FCSTD DOCUMENT  (FreeCAD 0.19R23578 (Git))
Label: printer_assembly_v2
License: All rights reserved
LicenseURL: http://en.wikipedia.org/wiki/All_rights_reserved
objects: App::Link×4, PartDesign::CoordinateSystem×1, App::DocumentObjectGroup×1, App::FeaturePython×1, App::Part×1
note: 1 computed .brp shape members not serialized (recipe doc carries the construction recipe); baked Part::Feature solids carry a one-line shape summary decoded from their .brp
EXTERNAL_REF file=base_plate.FCStd obj=LCS_2
EXTERNAL_REF file=base_plate.FCStd obj=Part014
EXTERNAL_REF file=base_plate.FCStd obj=LCS_1
EXTERNAL_REF file=frame_assembly.FCStd obj=LCS_Origin
EXTERNAL_REF file=frame_assembly.FCStd obj=Model
EXTERNAL_REF file=z_axis_assembly.FCStd obj=Model
EXTERNAL_REF file=enclosure_assembly.FCStd obj=LCS_Origin
EXTERNAL_REF file=enclosure_assembly.FCStd obj=Model

FEATURE [PartDesign::CoordinateSystem] LCS_Origin
  AttacherType = Attacher::AttachEngine3D
  MapMode = 2
  Support = -> [X_Axis]
FEATURE [App::DocumentObjectGroup] Constraints
FEATURE [App::FeaturePython] Variables  # WARN: FeaturePython — macro-defined, semantics opaque (R4)
FEATURE [App::Link] base_plate_base_plate
  AssemblyType = Asm4EE
  AttachedBy = #LCS_2
  AttachedTo = Parent Assembly#LCS_Origin
  AttachmentOffset = pos=(0,0,0) rot=(0,0,1;1.5708rad)
  LinkPlacement = pos=(-164.998,0.0367946,19.05) rot=(0,0,-1;0.00036rad)
  LinkedObject = -> <external base_plate.FCStd>#Part014
  Placement = pos=(-164.998,0.0367946,19.05) rot=(0,0,-1;0.00036rad)
  expr: Placement = LCS_Origin.Placement * AttachmentOffset * base_plate#LCS_2.Placement ^ -1
FEATURE [App::Link] frame_assembly
  AssemblyType = Asm4EE
  AttachedBy = #LCS_Origin
  AttachedTo = base_plate_base_plate#LCS_1
  AttachmentOffset = pos=(0,0,0) rot=(0,-0.707107,-0.707107;3.14159rad)
  LinkPlacement = pos=(-139.598,0.0276527,19.05) rot=(0,0,-1;0.00036rad)
  LinkedObject = -> <external frame_assembly.FCStd>#Model
  Placement = pos=(-139.598,0.0276527,19.05) rot=(0,0,-1;0.00036rad)
  expr: Placement = base_plate_base_plate.Placement * base_plate#LCS_1.Placement * AttachmentOffset * frame_assembly#LCS_Origin.Placement ^ -1
FEATURE [App::Link] z_axis_assembly
  LinkPlacement = pos=(-139.598,0.0275961,256.05) rot=(0.000331,0,-1;0.00036rad)
  LinkedObject = -> <external z_axis_assembly.FCStd>#Model
  Placement = pos=(-139.598,0.0275961,256.05) rot=(0.000331,0,-1;0.00036rad)
FEATURE [App::Link] enclosure_assembly
  AssemblyType = Asm4EE
  AttachedBy = #LCS_Origin
  AttachedTo = Parent Assembly#LCS_Origin
  AttachmentOffset = pos=(-166,0,20) rot=(0,0,1;0rad)
  LinkPlacement = pos=(-166,0,20) rot=(0,0,1;0rad)
  LinkedObject = -> <external enclosure_assembly.FCStd>#Model
  Placement = pos=(-166,0,20) rot=(0,0,1;0rad)
  expr: Placement = LCS_Origin.Placement * AttachmentOffset * enclosure_assembly#LCS_Origin.Placement ^ -1
FEATURE [App::Part] Model
  Configuration = 0
  Group = -> [LCS_Origin,Constraints,Variables,base_plate_base_plate,frame_assembly,z_axis_assembly,enclosure_assembly]
  Origin = -> Origin
  Type = Assembly4 Model

RESOLVED EXTERNAL PARTS (link-assembly join: the EXTERNAL_REF files above that resolve inside this repo's crawl, each included once):
---- part base_plate.FCStd = doc fcstd_9e080127ff6f ----
FCSTD DOCUMENT  (FreeCAD 0.19R23578 (Git))
Label: base_plate
License: All rights reserved
LicenseURL: http://en.wikipedia.org/wiki/All_rights_reserved
objects: Sketcher::SketchObject×5, PartDesign::Pocket×3, PartDesign::Pad×2, PartDesign::CoordinateSystem×2, PartDesign::Body×1, App::Part×1
note: 18 computed .brp shape members not serialized (recipe doc carries the construction recipe); baked Part::Feature solids carry a one-line shape summary decoded from their .brp

FEATURE [Sketcher::SketchObject] Sketch018
  MapMode = 5
  Support = -> [XY_Plane021]
  sketch-geometry (4):
    g0: LineSegment StartX=-63.5 StartY=177.8 StartZ=0 EndX=393.7 EndY=177.8 EndZ=0
    g1: LineSegment StartX=393.7 StartY=177.8 StartZ=0 EndX=393.7 EndY=-177.8 EndZ=0
    g2: LineSegment StartX=393.7 StartY=-177.8 StartZ=0 EndX=-63.5 EndY=-177.8 EndZ=0
    g3: LineSegment StartX=-63.5 StartY=-177.8 StartZ=0 EndX=-63.5 EndY=177.8 EndZ=0
  constraints (11):
    c: Coincident(g0,g1)
    c: Coincident(g1,g2)
    c: Coincident(g2,g3)
    c: Coincident(g3,g0)
    c: Horizontal(g0)
    c: Horizontal(g2)
    c: Vertical(g1)
    c: DistanceY(g-1,g0) = 177.8
    c: DistanceX(g0,g0) = 457.2
    c: DistanceX(g0,g-1) = 63.5
    c: Symmetric(g0,g2,g-1)
FEATURE [PartDesign::Pad] Pad008
  AllowMultiFace = false
  Direction = (1,1,1)
  Length = 19.05
  Length2 = 100
  Profile = -> Sketch018
  Reversed = true
  Type = 0
FEATURE [Sketcher::SketchObject] Sketch019
  MapMode = 5
  Support = -> [XY_Plane021]
  sketch-geometry (12):
    g0: LineSegment StartX=0 StartY=-127 StartZ=0 EndX=0 EndY=-177.8 EndZ=0
    g1: LineSegment StartX=0 StartY=-177.8 StartZ=0 EndX=-12.7 EndY=-177.8 EndZ=0
    g2: LineSegment StartX=-12.7 StartY=-177.8 StartZ=0 EndX=-12.7 EndY=-136.525 EndZ=0
    g3: LineSegment StartX=-63.5 StartY=-127 StartZ=0 EndX=-63.5 EndY=-136.525 EndZ=0
    g4: LineSegment StartX=-63.5 StartY=-136.525 StartZ=0 EndX=-12.7 EndY=-136.525 EndZ=0
    g5: LineSegment StartX=-63.5 StartY=-127 StartZ=0 EndX=0 EndY=-127 EndZ=0
    g6: LineSegment StartX=-12.7 StartY=136.525 StartZ=0 EndX=-63.5 EndY=136.525 EndZ=0
    g7: LineSegment StartX=-63.5 StartY=136.525 StartZ=0 EndX=-63.5 EndY=127 EndZ=0
    g8: LineSegment StartX=-63.5 StartY=127 StartZ=0 EndX=0 EndY=127 EndZ=0
    g9: LineSegment StartX=0 StartY=127 StartZ=0 EndX=0 EndY=177.8 EndZ=0
    g10: LineSegment StartX=0 StartY=177.8 StartZ=0 EndX=-12.7 EndY=177.8 EndZ=0
    g11: LineSegment StartX=-12.7 StartY=177.8 StartZ=0 EndX=-12.7 EndY=136.525 EndZ=0
  constraints (36):
    c: Coincident(g0,g1)
    c: Coincident(g1,g2)
    c: Horizontal(g1)
    c: Vertical(g0)
    c: Vertical(g2)
    c: Coincident(g3,g4)
    c: Horizontal(g4)
    c: Vertical(g3)
    c: Coincident(g2,g4)
    c: Coincident(g5,g3)
    c: Coincident(g5,g0)
    c: Horizontal(g5)
    c: DistanceY(g0,g-1) = 177.8
    c: DistanceX(g5,g5) = 63.5
    c: DistanceY(g3,g3) = 9.525
    c: PointOnObject(g0,g-2)
    c: DistanceY(g0,g0) = 50.8
    c: DistanceX(g1,g1) = 12.7
    c: Horizontal(g6)
    c: Coincident(g6,g7)
    c: Coincident(g7,g8)
    c: Coincident(g8,g9)
    c: Coincident(g9,g10)
    c: Coincident(g10,g11)
    c: Coincident(g11,g6)
    c: Vertical(g11)
    c: Vertical(g9)
    c: Vertical(g7)
    c: Horizontal(g10)
    c: Horizontal(g8)
    c: PointOnObject(g8,g-2)
    c: DistanceX(g10,g10) = 12.7
    c: DistanceX(g8,g8) = 63.5
    c: DistanceY(g9,g9) = 50.8
    c: DistanceY(g7,g7) = 9.525
    c: DistanceY(g-1,g9) = 177.8
FEATURE [PartDesign::Pad] Pad009
  AllowMultiFace = false
  BaseFeature = -> Pad008
  Direction = (1,1,1)
  Length = 127
  Length2 = 100
  Profile = -> Sketch019
  Type = 0
FEATURE [Sketcher::SketchObject] Sketch020
  MapMode = 5
  Placement = pos=(0,0,0) rot=(1,0,0;1.5708rad)
  Support = -> [XZ_Plane021]
  sketch-geometry (3):
    g0: LineSegment StartX=-63.5 StartY=0 StartZ=0 EndX=-12.7 EndY=127 EndZ=0
    g1: LineSegment StartX=-12.7 StartY=127 StartZ=0 EndX=-63.5 EndY=127 EndZ=0
    g2: LineSegment StartX=-63.5 StartY=127 StartZ=0 EndX=-63.5 EndY=0 EndZ=0
  constraints (9):
    c: Coincident(g0,g1)
    c: Horizontal(g1)
    c: Coincident(g1,g2)
    c: Coincident(g2,g0)
    c: Vertical(g2)
    c: PointOnObject(g0,g-1)
    c: DistanceY(g2,g2) = 127
    c: DistanceX(g0,g-1) = 12.7
    c: DistanceX(g0,g-1) = 63.5
FEATURE [PartDesign::Pocket] Pocket010
  AllowMultiFace = false
  BaseFeature = -> Pad009
  Length = 5
  Length2 = 100
  Midplane = true
  Profile = -> Sketch020
  Type = 1
FEATURE [Sketcher::SketchObject] Sketch021
  MapMode = 5
  Placement = pos=(0,0,0) rot=(0.57735,0.57735,0.57735;2.0944rad)
  Support = -> [YZ_Plane021]
  sketch-geometry (4):
    g0: Circle CenterX=-152.4 CenterY=101.6 CenterZ=0 NormalX=0 NormalY=0 NormalZ=1 AngleXU=0 Radius=6.35
    g1: Circle CenterX=-152.4 CenterY=25.4 CenterZ=0 NormalX=0 NormalY=0 NormalZ=1 AngleXU=0 Radius=6.35
    g2: Circle CenterX=152.4 CenterY=101.6 CenterZ=0 NormalX=0 NormalY=0 NormalZ=1 AngleXU=0 Radius=6.35
    g3: Circle CenterX=152.4 CenterY=25.4 CenterZ=0 NormalX=0 NormalY=0 NormalZ=1 AngleXU=0 Radius=6.35
  constraints (10):
    c: Symmetric(g1,g3,g-2)
    c: Symmetric(g0,g2,g-2)
    c: DistanceX(g0,g-1) = 152.4
    c: Vertical(g0,g1)
    c: Diameter(g0) = 12.7
    c: Equal(g0,g1)
    c: Equal(g1,g3)
    c: Equal(g3,g2)
    c: DistanceY(g-1,g0) = 101.6
    c: DistanceY(g-1,g1) = 25.4
FEATURE [PartDesign::Pocket] Pocket009
  AllowMultiFace = false
  BaseFeature = -> Pocket010
  Length = 5
  Length2 = 100
  Profile = -> Sketch021
  Type = 1
FEATURE [Sketcher::SketchObject] Sketch095
  MapMode = 5
  Support = -> [XY_Plane021]
  sketch-geometry (3):
    g0: Circle CenterX=245 CenterY=44 CenterZ=0 NormalX=0 NormalY=0 NormalZ=1 AngleXU=0 Radius=4
    g1: Circle CenterX=335 CenterY=-24 CenterZ=0 NormalX=0 NormalY=0 NormalZ=1 AngleXU=0 Radius=4
    g2: Circle CenterX=245 CenterY=-93 CenterZ=0 NormalX=0 NormalY=0 NormalZ=1 AngleXU=0 Radius=4
  constraints (9):
    c: Equal(g2,g0)
    c: Equal(g0,g1)
    c: Diameter(g1) = 8
    c: Vertical(g2,g0)
    c: DistanceY(g-1,g0) = 44
    c: DistanceX(g-1,g0) = 245
    c: DistanceY(g2,g-1) = 93
    c: DistanceX(g-1,g1) = 335
    c: DistanceY(g1,g-1) = 24
FEATURE [PartDesign::Pocket] Pocket
  BaseFeature = -> Pocket009
  Length = 5
  Length2 = 100
  Midplane = true
  Profile = -> Sketch095
  Type = 1
FEATURE [PartDesign::Body] Body008  label="Body"
  Group = -> [Sketch018,Pad008,Sketch019,Pad009,Sketch020,Pocket010,Sketch021,Pocket009,Sketch095,Pocket]
  Origin = -> Origin021
  Tip = -> Pocket
FEATURE [PartDesign::CoordinateSystem] LCS_1
  AttacherType = Attacher::AttachEngine3D
  AttachmentOffset = pos=(-25.4,0,0) rot=(0,0,1;0rad)
  MapMode = 45
  Placement = pos=(25.4,0,0) rot=(0,0.707107,0.707107;3.14159rad)
  Support = -> [Pocket]
FEATURE [PartDesign::CoordinateSystem] LCS_2
  AttacherType = Attacher::AttachEngine3D
  MapMode = 45
  Placement = pos=(164.998,0.0225906,-19.05) rot=(0,0,1;1.57116rad)
  Support = -> [Pocket]
FEATURE [App::Part] Part014  label="base_plate"
  Group = -> [Body008,LCS_1,LCS_2]
  Origin = -> Origin020
---- part enclosure_assembly.FCStd = doc fcstd_0174c90f82aa ----
FCSTD DOCUMENT  (FreeCAD 0.19R23578 (Git))
Label: enclosure_assembly
License: All rights reserved
LicenseURL: http://en.wikipedia.org/wiki/All_rights_reserved
objects: App::Link×8, App::DocumentObjectGroup×2, PartDesign::CoordinateSystem×1, App::FeaturePython×1, App::Part×1
note: 1 computed .brp shape members not serialized (recipe doc carries the construction recipe); baked Part::Feature solids carry a one-line shape summary decoded from their .brp
EXTERNAL_REF file=enclosure_sheetmetal.FCStd obj=LCS_4
EXTERNAL_REF file=enclosure_sheetmetal.FCStd obj=Body
EXTERNAL_REF file=enclosure_sheetmetal.FCStd obj=LCS_5
EXTERNAL_REF file=enclosure_windows.FCStd obj=LCS_1
EXTERNAL_REF file=enclosure_windows.FCStd obj=Body001
EXTERNAL_REF file=enclosure_hinges.FCStd obj=LCS_1
EXTERNAL_REF file=enclosure_sheetmetal.FCStd obj=LCS_7
EXTERNAL_REF file=enclosure_hinges.FCStd obj=Body001
EXTERNAL_REF file=enclosure_sheetmetal.FCStd obj=LCS_6
EXTERNAL_REF file=enclosure_hinges.FCStd obj=LCS_4
EXTERNAL_REF file=enclosure_hinges.FCStd obj=LCS_7
EXTERNAL_REF file=enclosure_hinges.FCStd obj=Body002
EXTERNAL_REF file=enclosure_hinges.FCStd obj=LCS_6
EXTERNAL_REF file=enclosure_sheetmetal.FCStd obj=LCS_3
EXTERNAL_REF file=enclosure_sheetmetal.FCStd obj=LCS_2
EXTERNAL_REF file=enclosure_sheetmetal.FCStd obj=Body001
EXTERNAL_REF file=enclosure_sheetmetal.FCStd obj=LCS_1
EXTERNAL_REF file=enclosure_windows.FCStd obj=LCS_2
EXTERNAL_REF file=enclosure_windows.FCStd obj=Body

FEATURE [App::DocumentObjectGroup] Parts
FEATURE [PartDesign::CoordinateSystem] LCS_Origin
  AttacherType = Attacher::AttachEngine3D
  MapMode = 2
  Support = -> [X_Axis]
FEATURE [App::DocumentObjectGroup] Constraints
FEATURE [App::FeaturePython] Variables  # WARN: FeaturePython — macro-defined, semantics opaque (R4)
FEATURE [App::Link] enclosure_sheetmetal_main_housing
  AssemblyType = Asm4EE
  AttachedBy = #LCS_4
  AttachedTo = Parent Assembly#LCS_Origin
  AttachmentOffset = pos=(0,0,0) rot=(0.707107,0,0.707107;3.14159rad)
  LinkPlacement = pos=(0,304.8,-3.73e-14) rot=(0.707107,0,0.707107;3.14159rad)
  LinkedObject = -> <external enclosure_sheetmetal.FCStd>#Body
  Placement = pos=(0,304.8,-3.73e-14) rot=(0.707107,0,0.707107;3.14159rad)
  expr: Placement = LCS_Origin.Placement * AttachmentOffset * enclosure_sheetmetal#LCS_4.Placement ^ -1
FEATURE [App::Link] enclosure_windows_top_acrylic_panel
  AssemblyType = Asm4EE
  AttachedBy = #LCS_1
  AttachedTo = enclosure_sheetmetal_main_housing#LCS_5
  AttachmentOffset = pos=(0,0,0) rot=(0,0,1;1.5708rad)
  LinkPlacement = pos=(298,2.6933e-12,573.5) rot=(0,0,-1;4.71239rad)
  LinkedObject = -> <external enclosure_windows.FCStd>#Body001
  Placement = pos=(298,2.6933e-12,573.5) rot=(0,0,-1;4.71239rad)
  expr: Placement = enclosure_sheetmetal_main_housing.Placement * enclosure_sheetmetal#LCS_5.Placement * AttachmentOffset * enclosure_windows#LCS_1.Placement ^ -1
FEATURE [App::Link] enclosure_hinges_Hinge_A
  AssemblyType = Asm4EE
  AttachedBy = #LCS_1
  AttachedTo = enclosure_sheetmetal_main_housing#LCS_7
  LinkPlacement = pos=(107.95,-306.8,514.35) rot=(-1,0,0;4.71239rad)
  LinkedObject = -> <external enclosure_hinges.FCStd>#Body001
  Placement = pos=(107.95,-306.8,514.35) rot=(-1,0,0;4.71239rad)
  expr: Placement = enclosure_sheetmetal_main_housing.Placement * enclosure_sheetmetal#LCS_7.Placement * AttachmentOffset * enclosure_hinges#LCS_1.Placement ^ -1
FEATURE [App::Link] enclosure_hinges_Hinge_A001
  AssemblyType = Asm4EE
  AttachedBy = #LCS_1
  AttachedTo = enclosure_sheetmetal_main_housing#LCS_6
  LinkPlacement = pos=(107.95,-306.8,95.25) rot=(-1,0,0;4.71239rad)
  LinkedObject = -> <external enclosure_hinges.FCStd>#Body001
  Placement = pos=(107.95,-306.8,95.25) rot=(-1,0,0;4.71239rad)
  expr: Placement = enclosure_sheetmetal_main_housing.Placement * enclosure_sheetmetal#LCS_6.Placement * AttachmentOffset * enclosure_hinges#LCS_1.Placement ^ -1
FEATURE [App::Link] enclosure_hinges_Hinge_B
  AssemblyType = Asm4EE
  AttachedBy = #LCS_7
  AttachedTo = enclosure_hinges_Hinge_A#LCS_4
  LinkPlacement = pos=(127,-325.85,476.25) rot=(0.57735,0.57735,-0.57735;4.18879rad)
  LinkedObject = -> <external enclosure_hinges.FCStd>#Body002
  Placement = pos=(127,-325.85,476.25) rot=(0.57735,0.57735,-0.57735;4.18879rad)
  expr: Placement = enclosure_hinges_Hinge_A.Placement * enclosure_hinges#LCS_4.Placement * AttachmentOffset * enclosure_hinges#LCS_7.Placement ^ -1
FEATURE [App::Link] enclosure_hinges_Hinge_B001
  AssemblyType = Asm4EE
  AttachedBy = #LCS_6
  AttachedTo = enclosure_sheetmetal_door#LCS_3
  AttachmentOffset = pos=(0,0,0) rot=(1,0,0;3.14159rad)
  LinkPlacement = pos=(127,-325.85,57.15) rot=(-0.57735,-0.57735,0.57735;2.0944rad)
  LinkedObject = -> <external enclosure_hinges.FCStd>#Body002
  Placement = pos=(127,-325.85,57.15) rot=(-0.57735,-0.57735,0.57735;2.0944rad)
  expr: Placement = enclosure_sheetmetal_door.Placement * enclosure_sheetmetal#LCS_3.Placement * AttachmentOffset * enclosure_hinges#LCS_6.Placement ^ -1
FEATURE [App::Link] enclosure_sheetmetal_door
  AssemblyType = Asm4EE
  AttachedBy = #LCS_2
  AttachedTo = enclosure_hinges_Hinge_B#LCS_6
  AttachmentOffset = pos=(0,0,0) rot=(1,0,0;3.14159rad)
  LinkPlacement = pos=(129,-346.9,571.5) rot=(1,0,0;4.71239rad)
  LinkedObject = -> <external enclosure_sheetmetal.FCStd>#Body001
  Placement = pos=(129,-346.9,571.5) rot=(1,0,0;4.71239rad)
  expr: Placement = enclosure_hinges_Hinge_B.Placement * enclosure_hinges#LCS_6.Placement * AttachmentOffset * enclosure_sheetmetal#LCS_2.Placement ^ -1
FEATURE [App::Link] enclosure_windows_side_acrylic_panel
  AssemblyType = Asm4EE
  AttachedBy = #LCS_2
  AttachedTo = enclosure_sheetmetal_door#LCS_1
  AttachmentOffset = pos=(0,0,0) rot=(0,0,1;3.14159rad)
  LinkPlacement = pos=(757.6,-346.9,284.75) rot=(0,-0.707107,-0.707107;3.14159rad)
  LinkedObject = -> <external enclosure_windows.FCStd>#Body
  Placement = pos=(757.6,-346.9,284.75) rot=(0,-0.707107,-0.707107;3.14159rad)
  expr: Placement = enclosure_sheetmetal_door.Placement * enclosure_sheetmetal#LCS_1.Placement * AttachmentOffset * enclosure_windows#LCS_2.Placement ^ -1
FEATURE [App::Part] Model
  Configuration = 0
  Group = -> [LCS_Origin,Constraints,Variables,enclosure_sheetmetal_main_housing,enclosure_windows_top_acrylic_panel,enclosure_hinges_Hinge_A,enclosure_hinges_Hinge_A001,enclosure_hinges_Hinge_B,enclosure_hinges_Hinge_B001,enclosure_sheetmetal_door,enclosure_windows_side_acrylic_panel]
  Origin = -> Origin
  Type = Assembly4 Model
---- part frame_assembly.FCStd = doc fcstd_40f002513768 ----
FCSTD DOCUMENT  (FreeCAD 0.19R23578 (Git))
Label: frame_assembly
License: All rights reserved
LicenseURL: http://en.wikipedia.org/wiki/All_rights_reserved
objects: App::Link×11, App::DocumentObjectGroup×2, PartDesign::CoordinateSystem×1, App::FeaturePython×1, App::Part×1
note: 1 computed .brp shape members not serialized (recipe doc carries the construction recipe); baked Part::Feature solids carry a one-line shape summary decoded from their .brp
EXTERNAL_REF file=frame_bottom_piece.FCStd obj=LCS_4
EXTERNAL_REF file=frame_bottom_piece.FCStd obj=Part008
EXTERNAL_REF file=frame_bottom_piece.FCStd obj=LCS_2
EXTERNAL_REF file=frame_side_piece.FCStd obj=LCS_2
EXTERNAL_REF file=frame_side_piece.FCStd obj=Part006
EXTERNAL_REF file=frame_bottom_piece.FCStd obj=LCS_1
EXTERNAL_REF file=frame_side_piece.FCStd obj=LCS_1
EXTERNAL_REF file=frame_top_piece.FCStd obj=LCS_2
EXTERNAL_REF file=frame_top_piece.FCStd obj=Part007
EXTERNAL_REF file=frame_top_piece.FCStd obj=LCS_3
EXTERNAL_REF file=z_motor_adaptor_plate.FCStd obj=LCS_1
EXTERNAL_REF file=z_motor_adaptor_plate.FCStd obj=Part
EXTERNAL_REF file=Nema 17  Stepper Motor length 60mm.FcStd obj=LCS_0
EXTERNAL_REF file=z_motor_adaptor_plate.FCStd obj=LCS_2
EXTERNAL_REF file=Nema 17  Stepper Motor length 60mm.FcStd obj=Part
EXTERNAL_REF file=Nema 17  Stepper Motor length 60mm.FcStd obj=LCS_1
EXTERNAL_REF file=5to8mm_spider_coupler.FCStd obj=LCS_1
EXTERNAL_REF file=5to8mm_spider_coupler.FCStd obj=CouplerASM
EXTERNAL_REF file=T8_leadscrew_l388mm.FCStd obj=LCS_1
EXTERNAL_REF file=T8_leadscrew_l388mm.FCStd obj=Part
EXTERNAL_REF file=KLF08_bearing_block.FCStd obj=LCS_1
EXTERNAL_REF file=frame_bottom_piece.FCStd obj=LCS_3
EXTERNAL_REF file=KLF08_bearing_block.FCStd obj=Part
EXTERNAL_REF file=12x500mm_linear_shaft.FCStd obj=LCS_1
EXTERNAL_REF file=frame_bottom_piece.FCStd obj=LCS_5
EXTERNAL_REF file=12x500mm_linear_shaft.FCStd obj=Part
EXTERNAL_REF file=frame_bottom_piece.FCStd obj=LCS_6

FEATURE [App::DocumentObjectGroup] Parts
FEATURE [PartDesign::CoordinateSystem] LCS_Origin
  AttacherType = Attacher::AttachEngine3D
  MapMode = 2
  Support = -> [X_Axis]
FEATURE [App::DocumentObjectGroup] Constraints
FEATURE [App::FeaturePython] Variables  # WARN: FeaturePython — macro-defined, semantics opaque (R4)
FEATURE [App::Link] frame_bottom_piece_frame_bottom_piece
  AssemblyType = Asm4EE
  AttachedBy = #LCS_4
  AttachedTo = Parent Assembly#LCS_Origin
  LinkPlacement = pos=(-25.4,0,0) rot=(0,0,1;0rad)
  LinkedObject = -> <external frame_bottom_piece.FCStd>#Part008
  Placement = pos=(-25.4,0,0) rot=(0,0,1;0rad)
  expr: Placement = LCS_Origin.Placement * AttachmentOffset * frame_bottom_piece#LCS_4.Placement ^ -1
FEATURE [App::Link] frame_side_piece_frame_side_piece
  AssemblyType = Asm4EE
  AttachedBy = #LCS_2
  AttachedTo = frame_bottom_piece_frame_bottom_piece#LCS_2
  AttachmentOffset = pos=(0,0,0) rot=(1,0,0;4.71239rad)
  LinkPlacement = pos=(25.4,127,50.8) rot=(0,0,-1;4.71239rad)
  LinkedObject = -> <external frame_side_piece.FCStd>#Part006
  Placement = pos=(25.4,127,50.8) rot=(0,0,-1;4.71239rad)
  expr: Placement = frame_bottom_piece_frame_bottom_piece.Placement * frame_bottom_piece#LCS_2.Placement * AttachmentOffset * frame_side_piece#LCS_2.Placement ^ -1
FEATURE [App::Link] frame_side_piece_frame_side_piece_2
  AssemblyType = Asm4EE
  AttachedBy = #LCS_2
  AttachedTo = frame_bottom_piece_frame_bottom_piece#LCS_1
  AttachmentOffset = pos=(0,0,0) rot=(1,0,0;4.71239rad)
  LinkPlacement = pos=(25.4,-177.8,50.8) rot=(0,0,-1;4.71239rad)
  LinkedObject = -> <external frame_side_piece.FCStd>#Part006
  Placement = pos=(25.4,-177.8,50.8) rot=(0,0,-1;4.71239rad)
  expr: Placement = frame_bottom_piece_frame_bottom_piece.Placement * frame_bottom_piece#LCS_1.Placement * AttachmentOffset * frame_side_piece#LCS_2.Placement ^ -1
FEATURE [App::Link] frame_top_piece_frame_top_piece
  AssemblyType = Asm4EE
  AttachedBy = #LCS_2
  AttachedTo = frame_side_piece_frame_side_piece#LCS_1
  AttachmentOffset = pos=(0,0,0) rot=(1,0,0;1.5708rad)
  LinkPlacement = pos=(-25.4,-5.68e-14,449.2) rot=(0,0,1;0rad)
  LinkedObject = -> <external frame_top_piece.FCStd>#Part007
  Placement = pos=(-25.4,-5.68e-14,449.2) rot=(0,0,1;0rad)
  expr: Placement = frame_side_piece_frame_side_piece.Placement * frame_side_piece#LCS_1.Placement * AttachmentOffset * frame_top_piece#LCS_2.Placement ^ -1
FEATURE [App::Link] z_motor_adaptor_plate_z_motor_adaptor_plate
  AssemblyType = Asm4EE
  AttachedBy = #LCS_1
  AttachedTo = frame_top_piece_frame_top_piece#LCS_3
  AttachmentOffset = pos=(0,0,0) rot=(0,0,1;4.71239rad)
  LinkPlacement = pos=(-2.238e-13,-5.68e-14,500) rot=(0,0,-1;1.5708rad)
  LinkedObject = -> <external z_motor_adaptor_plate.FCStd>#Part
  Placement = pos=(-2.238e-13,-5.68e-14,500) rot=(0,0,-1;1.5708rad)
  expr: Placement = frame_top_piece_frame_top_piece.Placement * frame_top_piece#LCS_3.Placement * AttachmentOffset * z_motor_adaptor_plate#LCS_1.Placement ^ -1
FEATURE [App::Link] Nema_17__Stepper_Motor_length_60mm_Nema_17__Stepper_Motor_length_60mm  label="Nema_17__Stepper_Motor_length_60mm_Nema 17  Stepper Motor length 60mm"
  AssemblyType = Asm4EE
  AttachedBy = #LCS_0
  AttachedTo = z_motor_adaptor_plate_z_motor_adaptor_plate#LCS_2
  AttachmentOffset = pos=(0,0,0) rot=(1,0,0;3.14159rad)
  LinkPlacement = pos=(-2.804e-13,-6.32e-14,565.75) rot=(1,0,0;1.5708rad)
  LinkedObject = -> <external Nema 17  Stepper Motor length 60mm.FcStd>#Part
  Placement = pos=(-2.804e-13,-6.32e-14,565.75) rot=(1,0,0;1.5708rad)
  expr: Placement = z_motor_adaptor_plate_z_motor_adaptor_plate.Placement * z_motor_adaptor_plate#LCS_2.Placement * AttachmentOffset * Nema_17__Stepper_Motor_length_60mm#LCS_0.Placement ^ -1
FEATURE [App::Link] _to8mm_spider_coupler_5to8mm_spider_coupler
  AssemblyType = Asm4EE
  AttachedBy = #LCS_1
  AttachedTo = Nema_17__Stepper_Motor_length_60mm_Nema_17__Stepper_Motor_length_60mm#LCS_1
  AttachmentOffset = pos=(0,0,0) rot=(0,1,0;3.14159rad)
  LinkPlacement = pos=(-2.101e-13,-4.47e-14,497.15) rot=(-0.085794,-0.7045,0.7045;2.97042rad)
  LinkedObject = -> <external 5to8mm_spider_coupler.FCStd>#CouplerASM
  Placement = pos=(-2.101e-13,-4.47e-14,497.15) rot=(-0.085794,-0.7045,0.7045;2.97042rad)
  expr: Placement = Nema_17__Stepper_Motor_length_60mm_Nema_17__Stepper_Motor_length_60mm.Placement * Nema_17__Stepper_Motor_length_60mm#LCS_1.Placement * AttachmentOffset * _to8mm_spider_coupler#LCS_1.Placement ^ -1
FEATURE [App::Link] T8_leadscrew_l388mm_T8_leadscrew_l388mm
  AssemblyType = Asm4EE
  AttachedBy = #LCS_1
  AttachedTo = _to8mm_spider_coupler_5to8mm_spider_coupler#LCS_1
  AttachmentOffset = pos=(0,0,0) rot=(0,-1,0;3.14159rad)
  LinkPlacement = pos=(-2.051e-13,-4.55e-14,482.15) rot=(0.707107,0.707107,0;3.14159rad)
  LinkedObject = -> <external T8_leadscrew_l388mm.FCStd>#Part
  Placement = pos=(-2.051e-13,-4.55e-14,482.15) rot=(0.707107,0.707107,0;3.14159rad)
  expr: Placement = _to8mm_spider_coupler_5to8mm_spider_coupler.Placement * _to8mm_spider_coupler#LCS_1.Placement * AttachmentOffset * T8_leadscrew_l388mm#LCS_1.Placement ^ -1
FEATURE [App::Link] KLF08_bearing_block_KLF08
  AssemblyType = Asm4EE
  AttachedBy = #LCS_1
  AttachedTo = frame_bottom_piece_frame_bottom_piece#LCS_3
  AttachmentOffset = pos=(0,0,0) rot=(1,0,0;3.14159rad)
  LinkPlacement = pos=(0,0,50.8) rot=(0.57735,0.57735,0.57735;2.0944rad)
  LinkedObject = -> <external KLF08_bearing_block.FCStd>#Part
  Placement = pos=(0,0,50.8) rot=(0.57735,0.57735,0.57735;2.0944rad)
  expr: Placement = frame_bottom_piece_frame_bottom_piece.Placement * frame_bottom_piece#LCS_3.Placement * AttachmentOffset * KLF08_bearing_block#LCS_1.Placement ^ -1
FEATURE [App::Link] _2x500mm_linear_shaft_12x500mm_linear_shaft
  AssemblyType = Asm4EE
  AttachedBy = #LCS_1
  AttachedTo = frame_bottom_piece_frame_bottom_piece#LCS_5
  LinkPlacement = pos=(13.4,-95.25,0) rot=(0,0,-1;1.5708rad)
  LinkedObject = -> <external 12x500mm_linear_shaft.FCStd>#Part
  Placement = pos=(13.4,-95.25,0) rot=(0,0,-1;1.5708rad)
  expr: Placement = frame_bottom_piece_frame_bottom_piece.Placement * frame_bottom_piece#LCS_5.Placement * AttachmentOffset * _2x500mm_linear_shaft#LCS_1.Placement ^ -1
FEATURE [App::Link] _2x500mm_linear_shaft_12x500mm_linear_shaft_2
  AssemblyType = Asm4EE
  AttachedBy = #LCS_1
  AttachedTo = frame_bottom_piece_frame_bottom_piece#LCS_6
  LinkPlacement = pos=(13.4,95.25,0) rot=(0,0,-1;1.5708rad)
  LinkedObject = -> <external 12x500mm_linear_shaft.FCStd>#Part
  Placement = pos=(13.4,95.25,0) rot=(0,0,-1;1.5708rad)
  expr: Placement = frame_bottom_piece_frame_bottom_piece.Placement * frame_bottom_piece#LCS_6.Placement * AttachmentOffset * _2x500mm_linear_shaft#LCS_1.Placement ^ -1
FEATURE [App::Part] Model
  Configuration = 0
  Group = -> [LCS_Origin,Constraints,Variables,frame_bottom_piece_frame_bottom_piece,frame_side_piece_frame_side_piece,frame_side_piece_frame_side_piece_2,frame_top_piece_frame_top_piece,z_motor_adaptor_plate_z_motor_adaptor_plate,Nema_17__Stepper_Motor_length_60mm_Nema_17__Stepper_Motor_length_60mm,_to8mm_spider_coupler_5to8mm_spider_coupler,T8_leadscrew_l388mm_T8_leadscrew_l388mm,KLF08_bearing_block_KLF08,+2 more]
  Origin = -> Origin
  Type = Assembly4 Model
---- part z_axis_assembly.FCStd = doc fcstd_634784b4e92b ----
FCSTD DOCUMENT  (FreeCAD 0.19R23578 (Git))
Label: z_axis_assembly
License: All rights reserved
LicenseURL: http://en.wikipedia.org/wiki/All_rights_reserved
objects: App::Link×12, App::DocumentObjectGroup×2, PartDesign::CoordinateSystem×2, App::FeaturePython×1, App::Part×1
note: 2 computed .brp shape members not serialized (recipe doc carries the construction recipe); baked Part::Feature solids carry a one-line shape summary decoded from their .brp
EXTERNAL_REF file=nut_block_t8_leadscrew.FCStd obj=LCS_1
EXTERNAL_REF file=nut_block_t8_leadscrew.FCStd obj=nut_block_t8_leadscrew
EXTERNAL_REF file=nut_block_standoff.FCStd obj=LCS_2
EXTERNAL_REF file=nut_block_t8_leadscrew.FCStd obj=LCS_0
EXTERNAL_REF file=nut_block_standoff.FCStd obj=Part018
EXTERNAL_REF file=nut_block_standoff.FCStd obj=LCS_1
EXTERNAL_REF file=z_axis_bearing_plate.FCStd obj=LCS_1
EXTERNAL_REF file=z_axis_bearing_plate.FCStd obj=Part017
EXTERNAL_REF file=SC12UU_bearing_block.FCStd obj=LCS_1
EXTERNAL_REF file=z_axis_bearing_plate.FCStd obj=LCS_2
EXTERNAL_REF file=SC12UU_bearing_block.FCStd obj=Part
EXTERNAL_REF file=z_axis_bearing_plate.FCStd obj=LCS_3
EXTERNAL_REF file=z_axis_bearing_plate.FCStd obj=LCS_4
EXTERNAL_REF file=z_axis_bearing_plate.FCStd obj=LCS_5
EXTERNAL_REF file=V-Slot 20x80x500 Linear Rail.FCStd obj=LCS_1
EXTERNAL_REF file=z_axis_bearing_plate.FCStd obj=LCS_6
EXTERNAL_REF file=V-Slot 20x80x500 Linear Rail.FCStd obj=Part
EXTERNAL_REF file=V-Slot 20x80x500 Linear Rail.FCStd obj=LCS_3
EXTERNAL_REF file=y_motor_bracket.FCStd obj=LCS_2
EXTERNAL_REF file=y_motor_bracket.FCStd obj=Part022
EXTERNAL_REF file=Nema 17  Stepper Motor length 60mm.FcStd obj=LCS_0
EXTERNAL_REF file=y_motor_bracket.FCStd obj=LCS_1
EXTERNAL_REF file=Nema 17  Stepper Motor length 60mm.FcStd obj=Part
EXTERNAL_REF file=Nema 17  Stepper Motor length 60mm.FcStd obj=LCS_1
EXTERNAL_REF file=2gt_pulley_20t.FCStd obj=LCS_1
EXTERNAL_REF file=2gt_pulley_20t.FCStd obj=Part
EXTERNAL_REF file=V-Slot 20x80x500 Linear Rail.FCStd obj=LCS_2
EXTERNAL_REF file=carriage_assembly.FCStd obj=LCS_1
EXTERNAL_REF file=carriage_assembly.FCStd obj=Model

FEATURE [App::DocumentObjectGroup] Parts
FEATURE [PartDesign::CoordinateSystem] LCS_Origin
  AttacherType = Attacher::AttachEngine3D
  MapMode = 2
  Support = -> [X_Axis]
FEATURE [App::DocumentObjectGroup] Constraints
FEATURE [App::FeaturePython] Variables  # WARN: FeaturePython — macro-defined, semantics opaque (R4)
FEATURE [App::Link] nut_block_t8_leadscrew_nut_block_t8_leadscrew
  AssemblyType = Asm4EE
  AttachedBy = #LCS_1
  AttachedTo = Parent Assembly#LCS_Origin
  AttachmentOffset = pos=(0,0,0) rot=(-1,0,0;4.71239rad)
  LinkPlacement = pos=(7.3e-15,5.3e-15,-10) rot=(0,0,1;4.71239rad)
  LinkedObject = -> <external nut_block_t8_leadscrew.FCStd>#nut_block_t8_leadscrew
  Placement = pos=(7.3e-15,5.3e-15,-10) rot=(0,0,1;4.71239rad)
  expr: Placement = LCS_Origin.Placement * AttachmentOffset * nut_block_t8_leadscrew#LCS_1.Placement ^ -1
FEATURE [App::Link] nut_block_standoff_nut_block_standoff
  AssemblyType = Asm4EE
  AttachedBy = #LCS_2
  AttachedTo = nut_block_t8_leadscrew_nut_block_t8_leadscrew#LCS_0
  AttachmentOffset = pos=(0,0,0) rot=(0,1,0;3.14159rad)
  LinkPlacement = pos=(28.4,6.44136e-07,6.5) rot=(-0.57735,-0.57735,0.57735;2.0944rad)
  LinkedObject = -> <external nut_block_standoff.FCStd>#Part018
  Placement = pos=(28.4,6.44136e-07,6.5) rot=(-0.57735,-0.57735,0.57735;2.0944rad)
  expr: Placement = nut_block_t8_leadscrew_nut_block_t8_leadscrew.Placement * nut_block_t8_leadscrew#LCS_0.Placement * AttachmentOffset * nut_block_standoff#LCS_2.Placement ^ -1
FEATURE [App::Link] z_axis_bearing_plate_bearing_plate
  AssemblyType = Asm4EE
  AttachedBy = #LCS_1
  AttachedTo = nut_block_standoff_nut_block_standoff#LCS_1
  AttachmentOffset = pos=(0,0,0) rot=(0,0,1;1.5708rad)
  LinkPlacement = pos=(28.4,6.44136e-07,6.5) rot=(0.57735,0.57735,0.57735;2.0944rad)
  LinkedObject = -> <external z_axis_bearing_plate.FCStd>#Part017
  Placement = pos=(28.4,6.44136e-07,6.5) rot=(0.57735,0.57735,0.57735;2.0944rad)
  expr: Placement = nut_block_standoff_nut_block_standoff.Placement * nut_block_standoff#LCS_1.Placement * AttachmentOffset * z_axis_bearing_plate#LCS_1.Placement ^ -1
FEATURE [App::Link] SC12UU_bearing_block_SC12UU_bearing_block
  AssemblyType = Asm4EE
  AttachedBy = #LCS_1
  AttachedTo = z_axis_bearing_plate_bearing_plate#LCS_2
  LinkPlacement = pos=(28.4,-95.25,-14.5) rot=(0,0,1;4.71239rad)
  LinkedObject = -> <external SC12UU_bearing_block.FCStd>#Part
  Placement = pos=(28.4,-95.25,-14.5) rot=(0,0,1;4.71239rad)
  expr: Placement = z_axis_bearing_plate_bearing_plate.Placement * z_axis_bearing_plate#LCS_2.Placement * AttachmentOffset * SC12UU_bearing_block#LCS_1.Placement ^ -1
FEATURE [App::Link] SC12UU_bearing_block_SC12UU_bearing_block_2
  AssemblyType = Asm4EE
  AttachedBy = #LCS_1
  AttachedTo = z_axis_bearing_plate_bearing_plate#LCS_3
  LinkPlacement = pos=(28.4,-95.25,27.5) rot=(0,0,1;4.71239rad)
  LinkedObject = -> <external SC12UU_bearing_block.FCStd>#Part
  Placement = pos=(28.4,-95.25,27.5) rot=(0,0,1;4.71239rad)
  expr: Placement = z_axis_bearing_plate_bearing_plate.Placement * z_axis_bearing_plate#LCS_3.Placement * AttachmentOffset * SC12UU_bearing_block#LCS_1.Placement ^ -1
FEATURE [App::Link] SC12UU_bearing_block_SC12UU_bearing_block_3
  AssemblyType = Asm4EE
  AttachedBy = #LCS_1
  AttachedTo = z_axis_bearing_plate_bearing_plate#LCS_4
  LinkPlacement = pos=(28.4,95.25,-14.5) rot=(0,0,1;4.71239rad)
  LinkedObject = -> <external SC12UU_bearing_block.FCStd>#Part
  Placement = pos=(28.4,95.25,-14.5) rot=(0,0,1;4.71239rad)
  expr: Placement = z_axis_bearing_plate_bearing_plate.Placement * z_axis_bearing_plate#LCS_4.Placement * AttachmentOffset * SC12UU_bearing_block#LCS_1.Placement ^ -1
FEATURE [App::Link] SC12UU_bearing_block_SC12UU_bearing_block_4
  AssemblyType = Asm4EE
  AttachedBy = #LCS_1
  AttachedTo = z_axis_bearing_plate_bearing_plate#LCS_5
  LinkPlacement = pos=(28.4,95.25,27.5) rot=(0,0,1;4.71239rad)
  LinkedObject = -> <external SC12UU_bearing_block.FCStd>#Part
  Placement = pos=(28.4,95.25,27.5) rot=(0,0,1;4.71239rad)
  expr: Placement = z_axis_bearing_plate_bearing_plate.Placement * z_axis_bearing_plate#LCS_5.Placement * AttachmentOffset * SC12UU_bearing_block#LCS_1.Placement ^ -1
FEATURE [App::Link] V_Slot_20x80x500_Linear_Rail_V_Slot_20x80x500_Linear_Rail  label="V_Slot_20x80x500_Linear_Rail_V-Slot 20x80x500 Linear Rail"
  AssemblyType = Asm4EE
  AttachedBy = #LCS_1
  AttachedTo = z_axis_bearing_plate_bearing_plate#LCS_6
  AttachmentOffset = pos=(0,0,0) rot=(0,0,1;1.5708rad)
  LinkPlacement = pos=(44.75,250,6.5) rot=(1,0,0;1.5708rad)
  LinkedObject = -> <external V-Slot 20x80x500 Linear Rail.FCStd>#Part
  Placement = pos=(44.75,250,6.5) rot=(1,0,0;1.5708rad)
  expr: Placement = z_axis_bearing_plate_bearing_plate.Placement * z_axis_bearing_plate#LCS_6.Placement * AttachmentOffset * V_Slot_20x80x500_Linear_Rail#LCS_1.Placement ^ -1
FEATURE [App::Link] y_motor_bracket_y_motor_bracket
  AssemblyType = Asm4EE
  AttachedBy = #LCS_2
  AttachedTo = V_Slot_20x80x500_Linear_Rail_V_Slot_20x80x500_Linear_Rail#LCS_3
  AttachmentOffset = pos=(0,0,0) rot=(0,0,1;4.71239rad)
  LinkPlacement = pos=(30.75,-252.5,18) rot=(0,0,1;0rad)
  LinkedObject = -> <external y_motor_bracket.FCStd>#Part022
  Placement = pos=(30.75,-252.5,18) rot=(0,0,1;0rad)
  expr: Placement = V_Slot_20x80x500_Linear_Rail_V_Slot_20x80x500_Linear_Rail.Placement * V_Slot_20x80x500_Linear_Rail#LCS_3.Placement * AttachmentOffset * y_motor_bracket#LCS_2.Placement ^ -1
FEATURE [App::Link] Nema_17__Stepper_Motor_length_60mm_Nema_17__Stepper_Motor_length_60mm  label="Nema_17__Stepper_Motor_length_60mm_Nema 17  Stepper Motor length 60mm"
  AssemblyType = Asm4EE
  AttachedBy = #LCS_0
  AttachedTo = y_motor_bracket_y_motor_bracket#LCS_1
  LinkPlacement = pos=(54.75,-274.5,81.4) rot=(-0.57735,0.57735,0.57735;4.18879rad)
  LinkedObject = -> <external Nema 17  Stepper Motor length 60mm.FcStd>#Part
  Placement = pos=(54.75,-274.5,81.4) rot=(-0.57735,0.57735,0.57735;4.18879rad)
  expr: Placement = y_motor_bracket_y_motor_bracket.Placement * y_motor_bracket#LCS_1.Placement * AttachmentOffset * Nema_17__Stepper_Motor_length_60mm#LCS_0.Placement ^ -1
FEATURE [App::Link] _gt_pulley_20t_2gt_pulley_20t
  AssemblyType = Asm4EE
  AttachedBy = #LCS_1
  AttachedTo = Nema_17__Stepper_Motor_length_60mm_Nema_17__Stepper_Motor_length_60mm#LCS_1
  AttachmentOffset = pos=(0,0,0) rot=(1,0,0;3.14159rad)
  LinkPlacement = pos=(54.75,-274.5,-2.2) rot=(0,-1,0;1.5708rad)
  LinkedObject = -> <external 2gt_pulley_20t.FCStd>#Part
  Placement = pos=(54.75,-274.5,-2.2) rot=(0,-1,0;1.5708rad)
  expr: Placement = Nema_17__Stepper_Motor_length_60mm_Nema_17__Stepper_Motor_length_60mm.Placement * Nema_17__Stepper_Motor_length_60mm#LCS_1.Placement * AttachmentOffset * _gt_pulley_20t#LCS_1.Placement ^ -1
FEATURE [App::Link] carriage_assembly
  AssemblyType = Asm4EE
  AttachedBy = #LCS_1
  AttachedTo = V_Slot_20x80x500_Linear_Rail_V_Slot_20x80x500_Linear_Rail#LCS_2
  LinkPlacement = pos=(56.25,1.2758e-06,6.5) rot=(0,0,1;0rad)
  LinkedObject = -> <external carriage_assembly.FCStd>#Model
  Placement = pos=(56.25,1.2758e-06,6.5) rot=(0,0,1;0rad)
  expr: Placement = V_Slot_20x80x500_Linear_Rail_V_Slot_20x80x500_Linear_Rail.Placement * V_Slot_20x80x500_Linear_Rail#LCS_2.Placement * AttachmentOffset * carriage_assembly#LCS_1.Placement ^ -1
FEATURE [PartDesign::CoordinateSystem] LCS_1
  AttacherType = Attacher::AttachEngine3D
  Placement = pos=(0,1e-15,2e-15) rot=(1,0,0;1.5708rad)
  expr: Placement = nut_block_t8_leadscrew_nut_block_t8_leadscrew.Placement * nut_block_t8_leadscrew#LCS_1.Placement * AttachmentOffset
FEATURE [App::Part] Model
  Configuration = 0
  Group = -> [LCS_Origin,Constraints,Variables,nut_block_t8_leadscrew_nut_block_t8_leadscrew,nut_block_standoff_nut_block_standoff,z_axis_bearing_plate_bearing_plate,SC12UU_bearing_block_SC12UU_bearing_block,SC12UU_bearing_block_SC12UU_bearing_block_2,SC12UU_bearing_block_SC12UU_bearing_block_3,SC12UU_bearing_block_SC12UU_bearing_block_4,V_Slot_20x80x500_Linear_Rail_V_Slot_20x80x500_Linear_Rail,+5 more]
  Origin = -> Origin
  Type = Assembly4 Model
